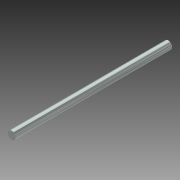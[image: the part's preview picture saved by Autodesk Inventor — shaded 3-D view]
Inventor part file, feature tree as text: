
AUTODESK INVENTOR PART (.ipt)
format: ipt  version: 2013 (Build 170138000, 138)  size: 67,072 bytes
history: native  units: in
note: dims shown in document units (in); Inventor stores cm internally (conversion verified against a paired STEP export)
features: extrude x1, sketch x1
ambient origin geometry x8: Origin, YZ Plane, XZ Plane, XY Plane, X Axis, Y Axis, Z Axis, Center Point
bodies: Solid1 (feature_tree)
feature tree (2):
  extrude  "Extrusion1"  Depth=2.5in TaperAngle=0.0deg
  sketch  "Sketch1"  dims[d0=0.125in d1=2.5in d2=0.0in]
